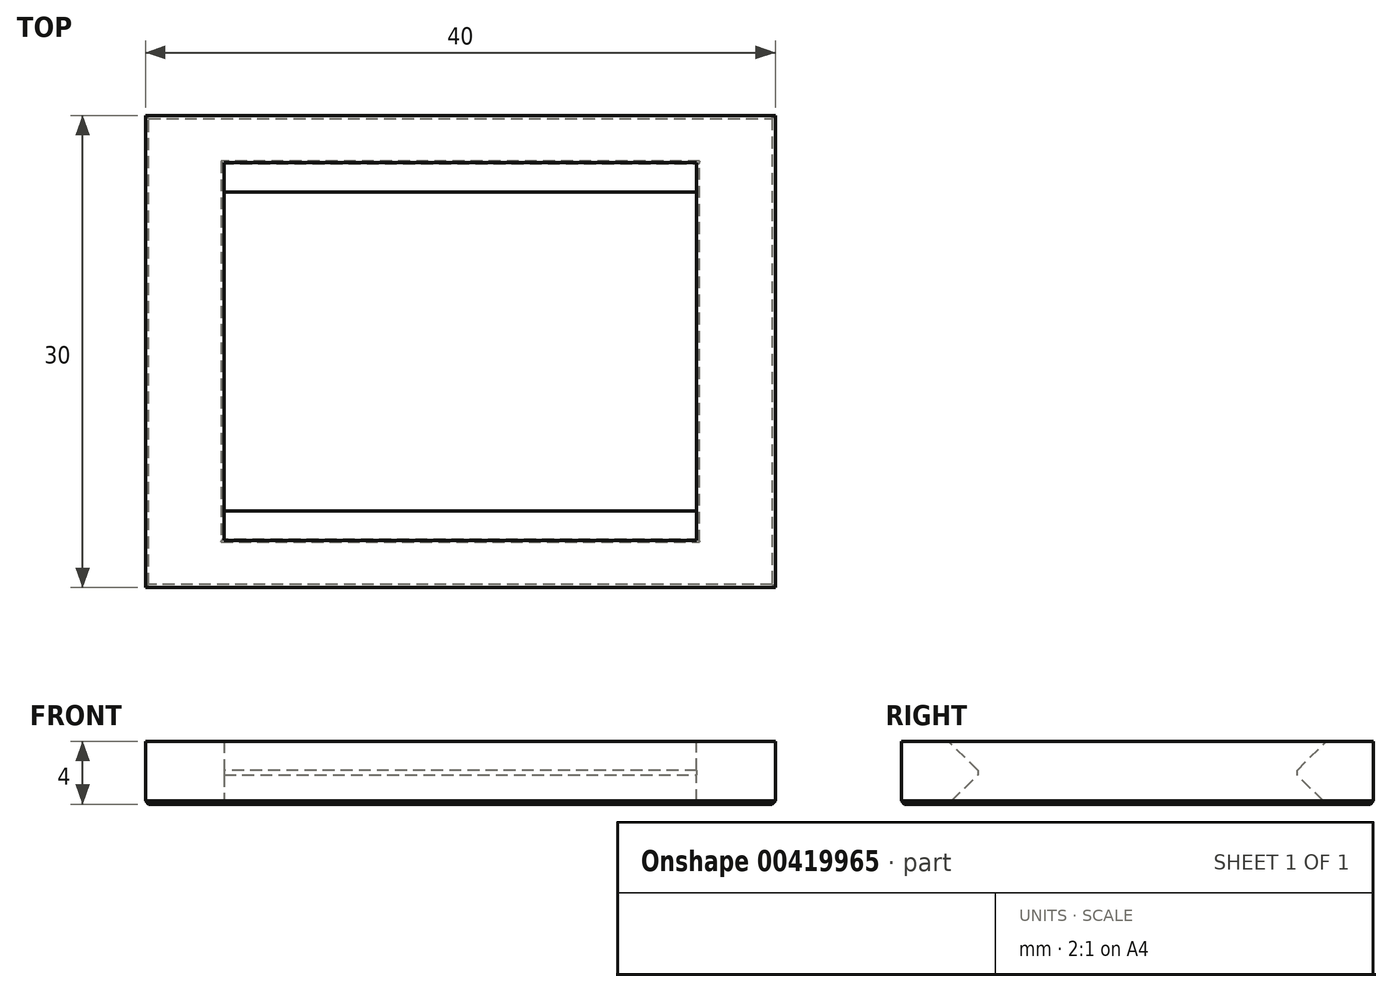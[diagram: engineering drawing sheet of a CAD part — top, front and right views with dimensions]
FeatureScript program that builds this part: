
annotation { "Feature Type Name" : "Feature", "Feature Type Description" : "" }
export const myFeature = defineFeature(function(context is Context, id is Id, definition is map)
    precondition{}
    {
        {
            var Q0;
            Q0=qCreatedBy(makeId("Top.planeOp"),FACE);
            var sketch = newSketch(context, id + "F0", { "sketchPlane" : qUnion([Q0])});
            skLineSegment(sketch, "E0.bottom", {"start": v(20, 15) * mm, "end": v(-20, 15) * mm});
            skLineSegment(sketch, "E0.top", {"start": v(20, -15) * mm, "end": v(-20, -15) * mm});
            skLineSegment(sketch, "E0.left", {"start": v(20, 15) * mm, "end": v(20, -15) * mm});
            skLineSegment(sketch, "E0.right", {"start": v(-20, 15) * mm, "end": v(-20, -15) * mm});
            skPoint(sketch, "E0.middle", {"position": v(0, 0) * mm});
            skLineSegment(sketch, "E1.bottom", {"start": v(15, 12) * mm, "end": v(-15, 12) * mm});
            skLineSegment(sketch, "E1.top", {"start": v(15, -12) * mm, "end": v(-15, -12) * mm});
            skLineSegment(sketch, "E1.left", {"start": v(15, 12) * mm, "end": v(15, -12) * mm});
            skLineSegment(sketch, "E1.right", {"start": v(-15, 12) * mm, "end": v(-15, -12) * mm});
            skSolve(sketch);
        }
        {
            var Q0;
            Q0=qCreatedBy(makeId("Front.planeOp"),FACE);
            var sketch = newSketch(context, id + "F1", { "sketchPlane" : qUnion([Q0])});
            skLineSegment(sketch, "E2", {"start": v(0, 0) * mm, "end": v(0, -4) * mm});
            skSolve(sketch);
        }
        {
            var Q0;
            Q0 = qSketchRegion(id + "F0", true);
            var Q1;
            Q1=sQuery(id+"F1.wireOp",EDGE,"E2");
            sweep(context, id + "F2", {"profiles" : qUnion([Q0]), "path" : qUnion([Q1])});
        }
        {
            var Q0;
            Q0=makeQuery(id+"F2.opSweep","SWEPT_FACE",FACE,{"disambiguationData":[OSD([sQuery(id+"F0.wireOp",EDGE,"E1.right"),sQuery(id+"F1.wireOp",EDGE,"E2")])]});
            var sketch = newSketch(context, id + "F3", { "sketchPlane" : qUnion([Q0])});
            skLineSegment(sketch, "E3.0.0", {"start": v(-12, 0) * mm, "end": v(-12, -4) * mm});
            skLineSegment(sketch, "E3.0.1", {"start": v(-12, -4) * mm, "end": v(12, -4) * mm, "construction": true});
            skLineSegment(sketch, "E3.0.2", {"start": v(12, -4) * mm, "end": v(12, 0) * mm});
            skLineSegment(sketch, "E3.0.3", {"start": v(12, 0) * mm, "end": v(-12, 0) * mm, "construction": true});
            skLineSegment(sketch, "E4", {"start": v(-12, 0) * mm, "end": v(-10, -2) * mm});
            skLineSegment(sketch, "E5", {"start": v(-10, -2) * mm, "end": v(-12, -4) * mm});
            skLineSegment(sketch, "E6.MirrorCS", {"start": v(12, 0) * mm, "end": v(10, -2) * mm});
            skLineSegment(sketch, "E7.MirrorCS", {"start": v(10, -2) * mm, "end": v(12, -4) * mm});
            skSolve(sketch);
        }
        {
            var Q0;
            Q0 = qSketchRegion(id + "F3", true);
            var Q1;
            Q1=makeQuery(id+"F2.opSweep","SWEPT_FACE",FACE,{"disambiguationData":[OSD([sQuery(id+"F0.wireOp",EDGE,"E1.left"),sQuery(id+"F1.wireOp",EDGE,"E2")])]});
            extrude(context, id + "F4", {"entities" : qUnion([Q0]), "operationType" : NewBodyOperationType.ADD, "endBound" : BoundingType.UP_TO_SURFACE, "endBoundEntityFace" : qUnion([Q1]), "depth" : 25 * mm});
        }
        {
            var Q0;
            Q0=makeQuery(id+"F4.opExtrude","SWEPT_EDGE",EDGE,{"disambiguationData":[OSD([sQuery(id+"F3.wireOp",EDGE,"E4"),sQuery(id+"F3.wireOp",EDGE,"E5")])]});
            var Q1;
            Q1=makeQuery(id+"F4.opExtrude","SWEPT_EDGE",EDGE,{"disambiguationData":[OSD([sQuery(id+"F3.wireOp",EDGE,"E6.MirrorCS"),sQuery(id+"F3.wireOp",EDGE,"E7.MirrorCS")])]});
            chamfer(context, id + "F5", {"entities" : qUnion([Q0, Q1]), "width" : 0.2 * mm});
        }
        {
            var Q0;
            Q0=makeQuery(id+"F2.opSweep","CAP_FACE",FACE,{"disambiguationData":[OSD([sQuery(id+"F0.wireOp",EDGE,"E0.bottom"),sQuery(id+"F0.wireOp",EDGE,"E0.top"),sQuery(id+"F0.wireOp",EDGE,"E0.left"),sQuery(id+"F0.wireOp",EDGE,"E0.right"),sQuery(id+"F0.wireOp",EDGE,"E1.bottom"),sQuery(id+"F0.wireOp",EDGE,"E1.top"),sQuery(id+"F0.wireOp",EDGE,"E1.left"),sQuery(id+"F0.wireOp",EDGE,"E1.right"),sQuery(id+"F1.wireOp",VERTEX,"E2.end")])],"isStart":false});
            chamfer(context, id + "F6", {"entities" : qUnion([Q0]), "width" : 0.2 * mm});
        }
    });
